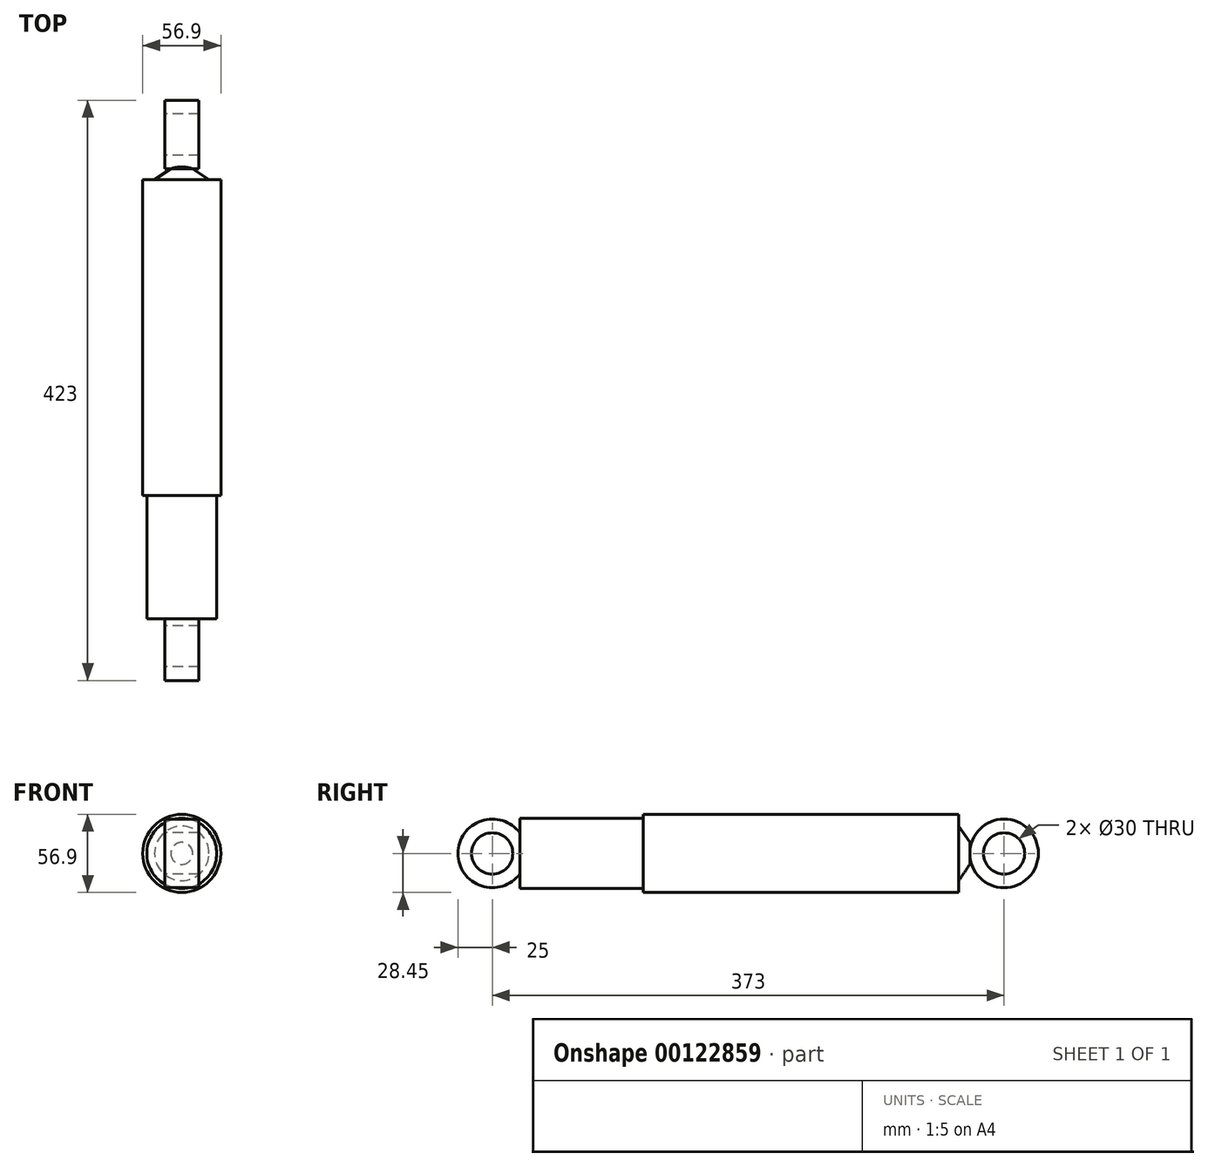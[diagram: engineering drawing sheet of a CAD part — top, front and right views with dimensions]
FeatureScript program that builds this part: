
annotation { "Feature Type Name" : "Feature", "Feature Type Description" : "" }
export const myFeature = defineFeature(function(context is Context, id is Id, definition is map)
    precondition{}
    {
        {
            var Q0;
            Q0=qCreatedBy(makeId("Front.planeOp"),FACE);
            var sketch = newSketch(context, id + "F0", { "sketchPlane" : qUnion([Q0])});
            skCircle(sketch, "E0", {"center": v(0, 0) * mm, "radius": 28.45 * mm});
            skSolve(sketch);
        }
        {
            var Q0;
            Q0=qSketchRegion(id+"F0",true);
            extrude(context, id + "F1", {"entities" : qUnion([Q0]), "depth" : 230 * mm});
        }
        {
            var Q0;
            Q0=makeQuery(id+"F1.opExtrude","CAP_FACE",FACE,{"disambiguationData":[OSD([sQuery(id+"F0.wireOp",EDGE,"E0")])],"isStart":false});
            var sketch = newSketch(context, id + "F2", { "sketchPlane" : qUnion([Q0])});
            skCircle(sketch, "E1", {"center": v(0, 0) * mm, "radius": 25.5 * mm});
            skSolve(sketch);
        }
        {
            var Q0;
            Q0=qSketchRegion(id+"F2",true);
            extrude(context, id + "F3", {"entities" : qUnion([Q0]), "operationType" : NewBodyOperationType.ADD, "depth" : 90 * mm});
        }
        {
            var Q0;
            Q0=qCreatedBy(makeId("Right.planeOp"),FACE);
            var sketch = newSketch(context, id + "F4", { "sketchPlane" : qUnion([Q0])});
            skLineSegment(sketch, "E2.0", {"start": v(-320, -25.5) * mm, "end": v(-320, 0) * mm, "construction": true});
            skPoint(sketch, "E3.endSnap0", {"position": v(-320, 0) * mm});
            skLineSegment(sketch, "E4", {"start": v(-285, 0) * mm, "end": v(-285, -21.45) * mm});
            skLineSegment(sketch, "E5", {"start": v(-285, -21.45) * mm, "end": v(-320, -25.5) * mm});
            skPoint(sketch, "E3.start.orphan", {"position": v(-320, 0) * mm});
            skPoint(sketch, "E6.end.orphan", {"position": v(-320, 25.5) * mm});
            skLineSegment(sketch, "E7", {"start": v(-320, 0) * mm, "end": v(-285, 0) * mm});
            skLineSegment(sketch, "E8", {"start": v(-320, 0) * mm, "end": v(-320, -25.5) * mm});
            skSolve(sketch);
        }
        {
            var Q0;
            Q0=qSketchRegion(id+"F4",true);
            var Q1;
            Q1=sQuery(id+"F4.wireOp",EDGE,"E7");
            revolve(context, id + "F5", {"operationType" : NewBodyOperationType.ADD, "entities" : qUnion([Q0]), "axis" : qUnion([Q1]), "revolveType" : RevolveType.FULL});
        }
        {
            var Q0;
            Q0=qCreatedBy(makeId("Right.planeOp"),FACE);
            var sketch = newSketch(context, id + "F6", { "sketchPlane" : qUnion([Q0])});
            skLineSegment(sketch, "E9.0", {"start": v(0, -28.45) * mm, "end": v(0, 28.45) * mm, "construction": true});
            skLineSegment(sketch, "E10", {"start": v(0, 0) * mm, "end": v(8, 0) * mm});
            skLineSegment(sketch, "E11", {"start": v(0, -28.45) * mm, "end": v(0, -19.82) * mm});
            skLineSegment(sketch, "E12", {"start": v(0, -19.82) * mm, "end": v(0, 0) * mm});
            skLineSegment(sketch, "E13", {"start": v(8, 0) * mm, "end": v(8, -8) * mm});
            skLineSegment(sketch, "E14", {"start": v(8, -8) * mm, "end": v(0, -19.82) * mm});
            skSolve(sketch);
        }
        {
            var Q0;
            Q0=qSketchRegion(id+"F6",true);
            var Q1;
            Q1=sQuery(id+"F6.wireOp",EDGE,"E10");
            revolve(context, id + "F7", {"operationType" : NewBodyOperationType.ADD, "entities" : qUnion([Q0]), "axis" : qUnion([Q1]), "revolveType" : RevolveType.FULL});
        }
        {
            var Q0;
            Q0=makeQuery(id+"F7.opRevolve","SWEPT_FACE",FACE,{"disambiguationData":[OSD([sQuery(id+"F6.wireOp",EDGE,"E13")])]});
            var sketch = newSketch(context, id + "F8", { "sketchPlane" : qUnion([Q0])});
            skCircle(sketch, "E15", {"center": v(0, 0) * mm, "radius": 8 * mm});
            skSolve(sketch);
        }
        {
            var Q0;
            Q0=qSketchRegion(id+"F8",true);
            extrude(context, id + "F9", {"entities" : qUnion([Q0]), "operationType" : NewBodyOperationType.ADD, "depth" : 5 * mm});
        }
        {
            var Q0;
            Q0=makeQuery(id+"F9.opExtrude","CAP_FACE",FACE,{"disambiguationData":[OSD([sQuery(id+"F8.wireOp",EDGE,"E15")])],"isStart":false});
            var sketch = newSketch(context, id + "F10", { "sketchPlane" : qUnion([Q0])});
            skCircle(sketch, "E16", {"center": v(0, 0) * mm, "radius": 6 * mm});
            skSolve(sketch);
        }
        {
            var Q0;
            Q0=qCreatedBy(makeId("Right.planeOp"),FACE);
            var sketch = newSketch(context, id + "F11", { "sketchPlane" : qUnion([Q0])});
            skLineSegment(sketch, "E17.0", {"start": v(-320, -25.5) * mm, "end": v(-320, 25.5) * mm, "construction": true});
            skLineSegment(sketch, "E18", {"start": v(-320, 0) * mm, "end": v(-340, 0) * mm, "construction": true});
            skCircle(sketch, "E19", {"center": v(-340, 0) * mm, "radius": 25 * mm});
            skCircle(sketch, "E20", {"center": v(-340, 0) * mm, "radius": 15 * mm});
            skLineSegment(sketch, "E21.0", {"start": v(13, 6) * mm, "end": v(13, -6) * mm, "construction": true});
            skLineSegment(sketch, "E22", {"start": v(13, 0) * mm, "end": v(33, 0) * mm, "construction": true});
            skPoint(sketch, "E22.endSnap0", {"position": v(13, 0) * mm});
            skCircle(sketch, "E23", {"center": v(33, 0) * mm, "radius": 25 * mm});
            skCircle(sketch, "E24", {"center": v(33, 0) * mm, "radius": 15 * mm});
            skSolve(sketch);
        }
        {
            var Q0;
            Q0 = qSketchRegion(id + "F11", true);
            extrude(context, id + "F12", {"entities" : qUnion([Q0]), "operationType" : NewBodyOperationType.ADD, "endBound" : BoundingType.SYMMETRIC, "depth" : 25 * mm});
        }
    });
